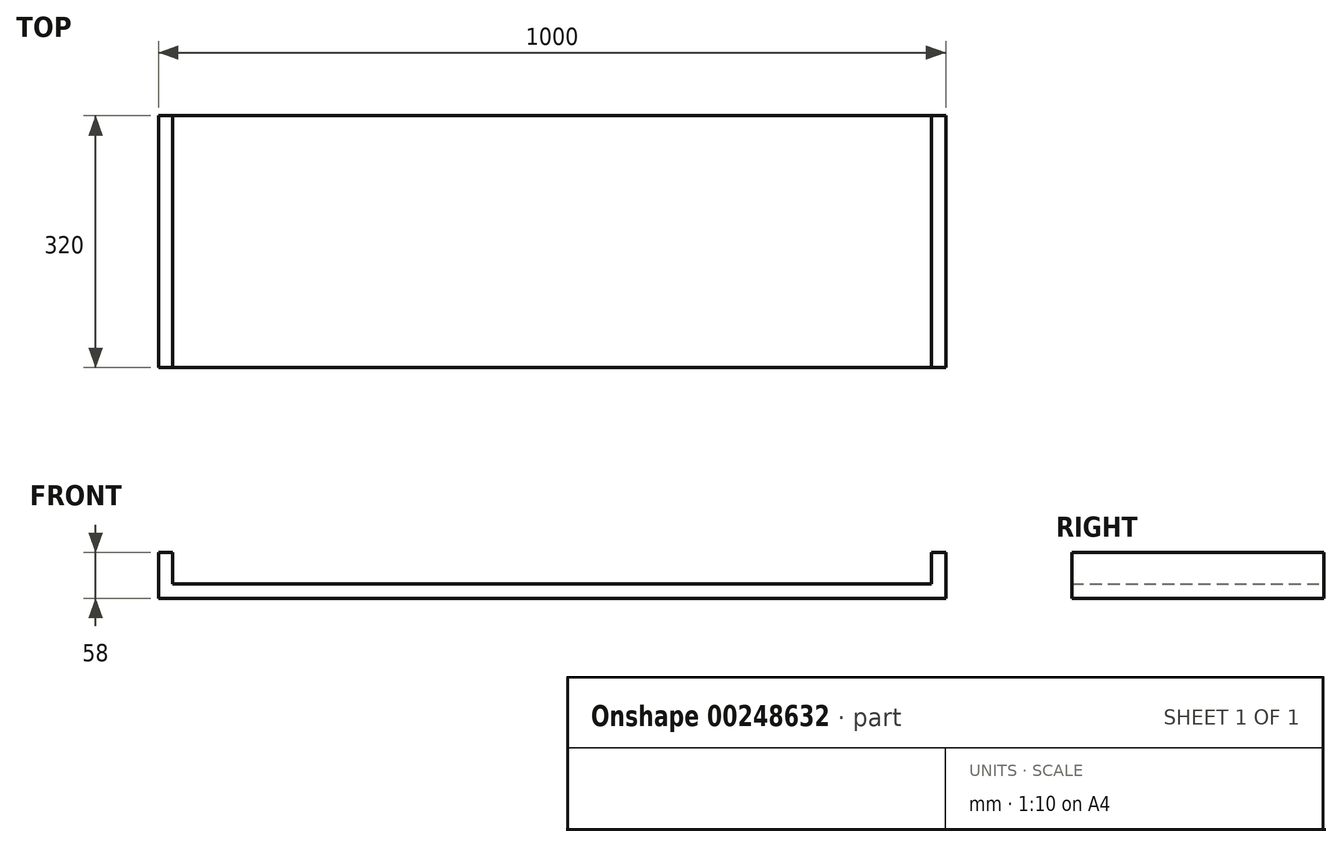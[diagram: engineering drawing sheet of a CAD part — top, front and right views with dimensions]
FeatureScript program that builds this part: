
annotation { "Feature Type Name" : "Feature", "Feature Type Description" : "" }
export const myFeature = defineFeature(function(context is Context, id is Id, definition is map)
    precondition{}
    {
        {
            var Q0;
            Q0=qCreatedBy(makeId("Front.planeOp"),FACE);
            var sketch = newSketch(context, id + "F0", { "sketchPlane" : qUnion([Q0])});
            skLineSegment(sketch, "E0.bottom", {"start": v(-478.6, 14.67) * mm, "end": v(485.4, 14.67) * mm});
            skLineSegment(sketch, "E0.top", {"start": v(-496.6, -3.33) * mm, "end": v(503.4, -3.33) * mm});
            skLineSegment(sketch, "E0.left", {"start": v(-496.6, 14.67) * mm, "end": v(-496.6, -3.33) * mm});
            skLineSegment(sketch, "E0.right", {"start": v(503.4, 14.67) * mm, "end": v(503.4, -3.33) * mm});
            skLineSegment(sketch, "E1.top", {"start": v(-496.6, 54.67) * mm, "end": v(-478.6, 54.67) * mm});
            skLineSegment(sketch, "E1.left", {"start": v(-496.6, 14.67) * mm, "end": v(-496.6, 54.67) * mm});
            skLineSegment(sketch, "E1.right", {"start": v(-478.6, 14.67) * mm, "end": v(-478.6, 54.67) * mm});
            skLineSegment(sketch, "E2.top", {"start": v(503.4, 54.67) * mm, "end": v(485.4, 54.67) * mm});
            skLineSegment(sketch, "E2.left", {"start": v(503.4, 14.67) * mm, "end": v(503.4, 54.67) * mm});
            skLineSegment(sketch, "E2.right", {"start": v(485.4, 14.67) * mm, "end": v(485.4, 54.67) * mm});
            skSolve(sketch);
        }
        {
            var Q0;
            Q0 = qSketchRegion(id + "F0", true);
            extrude(context, id + "F1", {"entities" : qUnion([Q0]), "depth" : 320 * mm});
        }
    });
